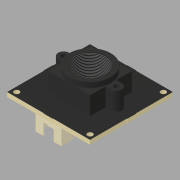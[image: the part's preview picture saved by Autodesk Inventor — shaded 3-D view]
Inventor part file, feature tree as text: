
AUTODESK INVENTOR PART (.ipt)
format: ipt  version: 2019 (Build 230136000, 136)  size: 276,992 bytes
history: native  units: mm
features: extrude x7, sketch x7, projected_geometry x2, fillet x1, thread x1
ambient origin geometry x8: Origin, YZ Plane, XZ Plane, XY Plane, X Axis, Y Axis, Z Axis, Center Point
bodies: Solid1 (feature_tree), Solid2 (feature_tree), Solid3 (feature_tree)
feature tree (18):
  extrude  "Extrusion1"  Depth=2.0mm
  fillet  "Fillet1"  Radius=2.0mm
  extrude  "Extrusion2"  Depth=2.0mm
  extrude  "Extrusion3"  Depth=2.0mm
  extrude  "Extrusion4"  Depth=2.0mm
  extrude  "Extrusion5"  Depth=2.0mm
  extrude  "Extrusion6"  Depth=3.0mm
  thread  "Thread1"  [1 undecoded]
  extrude  "Extrusion7"  Depth=0.5mm
  sketch  "Sketch1"  dims[d0=38.0mm d1=38.0mm d2=2.0mm]
  sketch  "Sketch2"  dims[d3=1.0mm d4=2.0mm]
  sketch  "Sketch3"  dims[d5=2.0mm d6=2.0mm]
  sketch  "Sketch4"  dims[d7=2.0mm d8=1.85mm]
  projected_geometry  "Projected Loop1"
  sketch  "Sketch5"  dims[d9=1.85mm d10=2.0mm]
  sketch  "Sketch6"  dims[d11=40.0mm d13=360.0deg d15=3.0mm d16=40.0mm d18=360.0deg]
  projected_geometry  "Projected Loop2"
  sketch  "Sketch7"  dims[d20=1.65mm d21=0.0mm d22=0.5mm d23=16.15mm d24=16.15mm d25=2.1mm d26=2.1mm d27=4.2mm d28=4.2mm d29=4.2mm d30=4.2mm d31=2.1mm d32=7.0mm d33=0.0mm d34=1.75mm d35=1.75mm d36=10.0mm d37=4.7mm d38=5.0mm d39=6.0mm d40=0.0mm d41=0.5mm d42=4.0mm d43=2.0mm d44=4.5mm d45=0.0mm d46=16.0mm d47=2.0mm d48=0.0mm d49=2.0mm d50=9.0mm d51=0.0mm d52=10.0mm d53=0.0mm d54=0.15mm d55=5.0mm d56=10.0mm d57=0.0mm]
note: 1 required parameter value undecoded (feature->parameter linkage not recoverable at this tier; creation-order binding heuristic only, values carry confidence <= 0.55)
